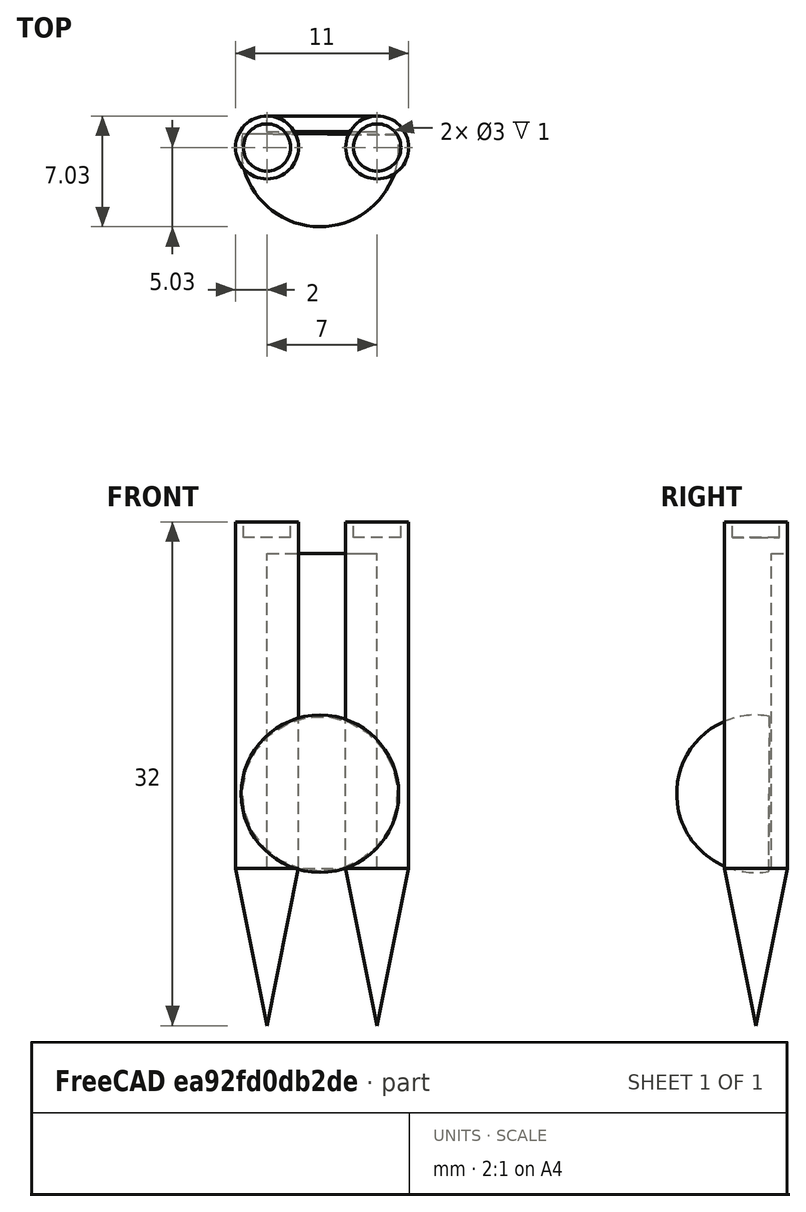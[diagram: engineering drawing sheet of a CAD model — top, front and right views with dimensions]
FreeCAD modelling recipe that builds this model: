
FCSTD DOCUMENT  (FreeCAD 0.14R3702 (Git))
Label: Playing Around With FreeCAD
License: CC-BY 3.0
LicenseURL: http://creativecommons.org/licenses/by/3.0/
objects: Part::Cylinder×4, Part::Cone×2, Part::Cut×2, Part::MultiFuse×2, Part::Box×1, Part::Sphere×1
note: 12 computed .brp shape members not serialized (recipe doc carries the construction recipe); baked Part::Feature solids carry a one-line shape summary decoded from their .brp

FEATURE [Part::Cylinder] Cylinder
  Angle = 360
  Height = 20
  Radius = 2
FEATURE [Part::Cone] Cone
  Angle = 360
  Height = 10
  Placement = pos=(0,0,-10) rot=(0,0,1;0rad)
  Radius1 = 0
  Radius2 = 2
FEATURE [Part::Cylinder] Cylinder001
  Angle = 360
  Height = 2
  Placement = pos=(1,11,9) rot=(0,0,1;0rad)
  Radius = 2
FEATURE [Part::Cylinder] Cylinder002
  Angle = 360
  Height = 1
  Placement = pos=(1,11,10) rot=(0,0,1;0rad)
  Radius = 1.5
FEATURE [Part::Cut] Cut
  Base = -> Cylinder001
  Placement = pos=(-1,-11,11) rot=(0,0,1;0rad)
  Tool = -> Cylinder002
FEATURE [Part::MultiFuse] Fusion
  Shapes = -> [Cut,Cylinder,Cone]
FEATURE [Part::Cone] Cone001
  Angle = 360
  Height = 10
  Placement = pos=(0,0,-10) rot=(0,0,1;0rad)
  Radius1 = 0
  Radius2 = 2
FEATURE [Part::Cylinder] Cylinder003
  Angle = 360
  Height = 20
  Radius = 2
FEATURE [Part::Cut] Cut001
  Base = -> Cylinder001
  Placement = pos=(-1,-11,11) rot=(0,0,1;0rad)
  Tool = -> Cylinder002
FEATURE [Part::MultiFuse] Fusion001
  Placement = pos=(-7,0,0) rot=(0,0,1;0rad)
  Shapes = -> [Cut001,Cylinder003,Cone001]
FEATURE [Part::Box] Box  label="Cube"
  Height = 20
  Length = 7
  Placement = pos=(-7,1,0) rot=(0,0,1;0rad)
  Width = 1
FEATURE [Part::Sphere] Sphere
  Angle1 = -90
  Angle2 = 10
  Angle3 = 360
  Placement = pos=(-3.63673,-0.0294058,4.72587) rot=(-0.583337,0.577512,0.571137;2.08621rad)
  Radius = 5
